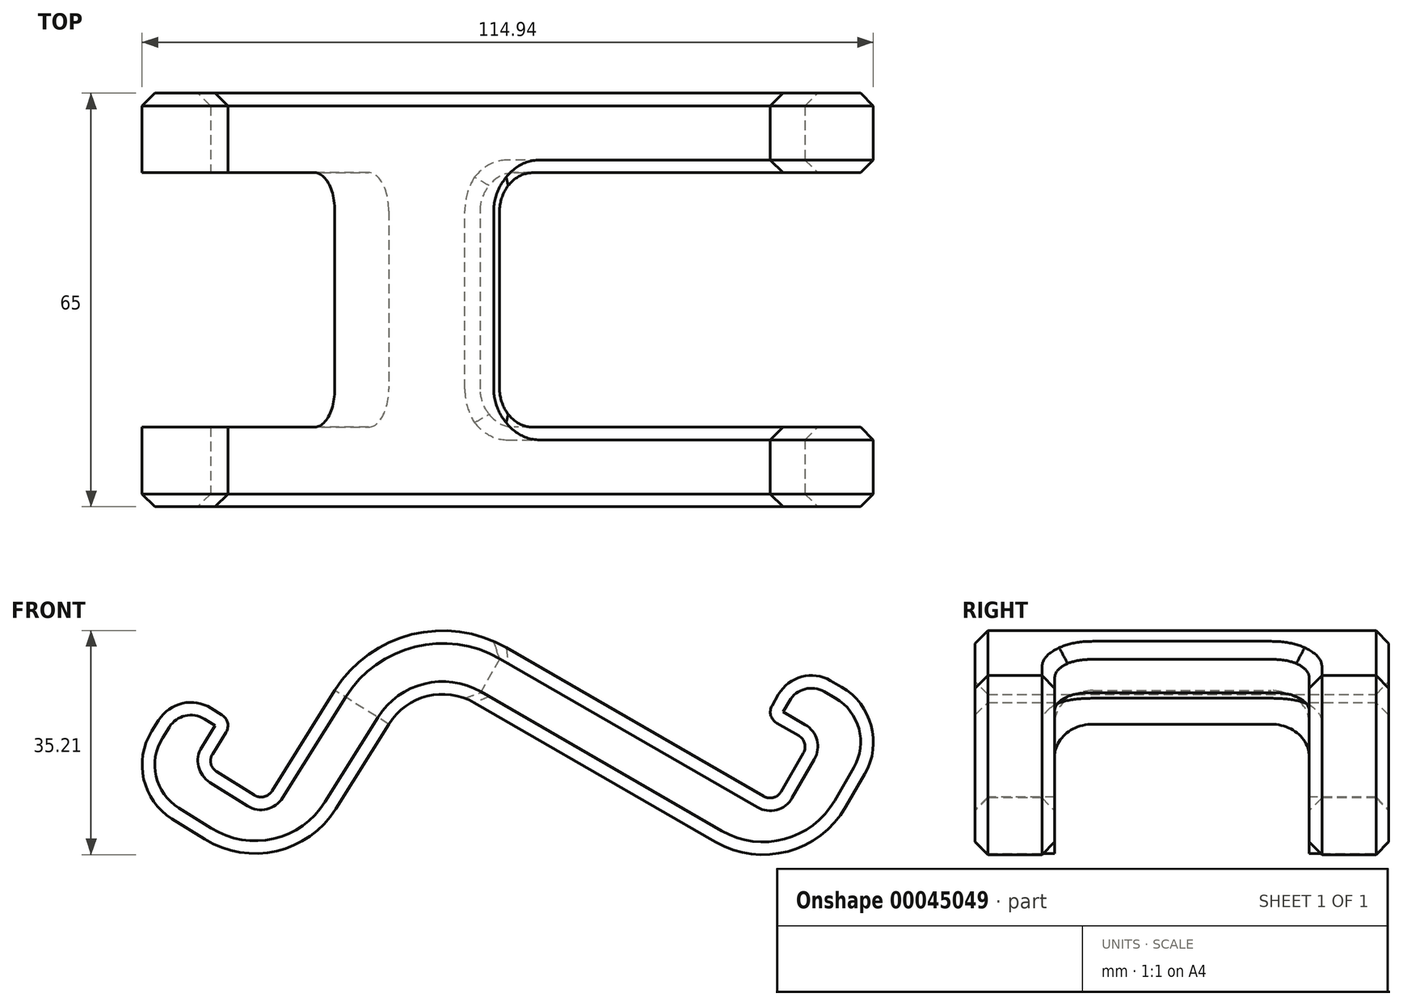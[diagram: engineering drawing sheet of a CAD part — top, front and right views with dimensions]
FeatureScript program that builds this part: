
annotation { "Feature Type Name" : "Feature", "Feature Type Description" : "" }
export const myFeature = defineFeature(function(context is Context, id is Id, definition is map)
    precondition{}
    {
        {
            var Q0;
            Q0=qCreatedBy(makeId("Front.planeOp"),FACE);
            var sketch = newSketch(context, id + "F0", { "sketchPlane" : qUnion([Q0])});
            skLineSegment(sketch, "E0", {"start": v(-41.48, 31.7) * mm, "end": v(-45.72, 24.9) * mm});
            skLineSegment(sketch, "E1", {"start": v(-42.54, 11.13) * mm, "end": v(-37.45, 7.95) * mm});
            skLineSegment(sketch, "E2", {"start": v(-16.78, 12.72) * mm, "end": v(-8.48, 26) * mm});
            skLineSegment(sketch, "E3", {"start": v(5, 29.36) * mm, "end": v(42.87, 7.5) * mm});
            skLineSegment(sketch, "E4", {"start": v(63.36, 13) * mm, "end": v(66.36, 18.19) * mm});
            skLineSegment(sketch, "E5", {"start": v(62.7, 31.85) * mm, "end": v(55.77, 35.85) * mm});
            skLineSegment(sketch, "E6", {"start": v(55.77, 35.85) * mm, "end": v(50.77, 27.19) * mm});
            skLineSegment(sketch, "E7", {"start": v(50.77, 27.19) * mm, "end": v(57.7, 23.19) * mm});
            skLineSegment(sketch, "E8", {"start": v(57.7, 23.19) * mm, "end": v(52.2, 13.66) * mm});
            skLineSegment(sketch, "E9", {"start": v(52.2, 13.66) * mm, "end": v(10, 38.02) * mm});
            skLineSegment(sketch, "E10", {"start": v(-16.96, 31.3) * mm, "end": v(-27.9, 13.78) * mm});
            skLineSegment(sketch, "E11", {"start": v(-27.9, 13.78) * mm, "end": v(-37.24, 19.6) * mm});
            skLineSegment(sketch, "E12", {"start": v(-37.24, 19.6) * mm, "end": v(-33, 26.4) * mm});
            skLineSegment(sketch, "E13", {"start": v(-33, 26.4) * mm, "end": v(-41.48, 31.7) * mm});
            skPoint(sketch, "E14.visualSharp", {"position": v(-6.73, 47.68) * mm});
            skArc(sketch, "E14.filletArc", {"start": v(10, 38.02) * mm, "mid": v(-4.84, 40.1) * mm, "end": v(-16.96, 31.3) * mm});
            skPoint(sketch, "E15.visualSharp", {"position": v(-3.36, 34.19) * mm});
            skArc(sketch, "E15.filletArc", {"start": v(5, 29.36) * mm, "mid": v(-2.42, 30.4) * mm, "end": v(-8.48, 26) * mm});
            skPoint(sketch, "E16.visualSharp", {"position": v(55.86, 0) * mm});
            skArc(sketch, "E16.filletArc", {"start": v(42.87, 7.5) * mm, "mid": v(54.25, 6) * mm, "end": v(63.36, 13) * mm});
            skPoint(sketch, "E17.visualSharp", {"position": v(-24.73, 0) * mm});
            skArc(sketch, "E17.filletArc", {"start": v(-37.45, 7.95) * mm, "mid": v(-26.13, 6.05) * mm, "end": v(-16.78, 12.72) * mm});
            skPoint(sketch, "E18.visualSharp", {"position": v(-51.02, 16.43) * mm});
            skArc(sketch, "E18.filletArc", {"start": v(-45.72, 24.9) * mm, "mid": v(-46.98, 17.36) * mm, "end": v(-42.54, 11.13) * mm});
            skPoint(sketch, "E19.visualSharp", {"position": v(71.36, 26.85) * mm});
            skArc(sketch, "E19.filletArc", {"start": v(66.36, 18.19) * mm, "mid": v(67.35, 25.77) * mm, "end": v(62.7, 31.85) * mm});
            skSolve(sketch);
        }
        {
            var Q0;
            Q0=qSketchRegion(id+"F0",true);
            extrude(context, id + "F1", {"entities" : qUnion([Q0]), "endBound" : BoundingType.SYMMETRIC, "depth" : 65 * mm});
        }
        {
            var Q0;
            Q0=qCreatedBy(makeId("Front.planeOp"),FACE);
            var sketch = newSketch(context, id + "F2", { "sketchPlane" : qUnion([Q0])});
            skLineSegment(sketch, "E20", {"start": v(5, 29.36) * mm, "end": v(55.86, 0) * mm});
            skLineSegment(sketch, "E21", {"start": v(55.86, 0) * mm, "end": v(71.36, 26.85) * mm});
            skLineSegment(sketch, "E22", {"start": v(71.36, 26.85) * mm, "end": v(20.5, 56.2) * mm});
            skLineSegment(sketch, "E23", {"start": v(20.5, 56.2) * mm, "end": v(5, 29.36) * mm});
            skLineSegment(sketch, "E24", {"start": v(-8.48, 26) * mm, "end": v(-34.77, 42.43) * mm});
            skLineSegment(sketch, "E25", {"start": v(-34.77, 42.43) * mm, "end": v(-51.02, 16.43) * mm});
            skLineSegment(sketch, "E26", {"start": v(-51.02, 16.43) * mm, "end": v(-24.73, 0) * mm});
            skLineSegment(sketch, "E27", {"start": v(-24.73, 0) * mm, "end": v(-8.48, 26) * mm});
            skLineSegment(sketch, "E28", {"start": v(-8.48, 26) * mm, "end": v(-8.48, 26) * mm});
            skLineSegment(sketch, "E29", {"start": v(5, 29.36) * mm, "end": v(5, 29.36) * mm});
            skSolve(sketch);
        }
        {
            var Q0;
            Q0=qSketchRegion(id+"F2",true);
            extrude(context, id + "F3", {"entities" : qUnion([Q0]), "operationType" : NewBodyOperationType.REMOVE, "endBound" : BoundingType.SYMMETRIC, "oppositeDirection" : true, "depth" : 40 * mm});
        }
        {
            var Q0;
            {var subQ0=sQuery(id+"F0.wireOp",EDGE,"E8");var subQ1=sQuery(id+"F0.wireOp",EDGE,"E9");Q0=makeQuery(id+"F3.boolean.opBoolean","SPLIT",EDGE,{"disambiguationData":[TD([makeQuery(id+"F3.opExtrude","CAP_FACE",FACE,{"disambiguationData":[OSD([sQuery(id+"F2.wireOp",EDGE,"E20"),sQuery(id+"F2.wireOp",EDGE,"E21"),sQuery(id+"F2.wireOp",EDGE,"E22"),sQuery(id+"F2.wireOp",EDGE,"E23")])],"isStart":false})])],"derivedFrom":makeQuery(id+"F1.opExtrude","SWEPT_EDGE",EDGE,{"disambiguationData":[OSD([subQ0,subQ1])]})});}
            var Q1;
            {var subQ0=sQuery(id+"F0.wireOp",EDGE,"E8");var subQ1=sQuery(id+"F0.wireOp",EDGE,"E9");Q1=makeQuery(id+"F3.boolean.opBoolean","SPLIT",EDGE,{"disambiguationData":[TD([makeQuery(id+"F3.opExtrude","CAP_FACE",FACE,{"disambiguationData":[OSD([sQuery(id+"F2.wireOp",EDGE,"E20"),sQuery(id+"F2.wireOp",EDGE,"E21"),sQuery(id+"F2.wireOp",EDGE,"E22"),sQuery(id+"F2.wireOp",EDGE,"E23")])],"isStart":true})])],"derivedFrom":makeQuery(id+"F1.opExtrude","SWEPT_EDGE",EDGE,{"disambiguationData":[OSD([subQ0,subQ1])]})});}
            var Q2;
            {var subQ0=sQuery(id+"F0.wireOp",EDGE,"E7");var subQ1=sQuery(id+"F0.wireOp",EDGE,"E8");Q2=makeQuery(id+"F3.boolean.opBoolean","SPLIT",EDGE,{"disambiguationData":[TD([makeQuery(id+"F3.opExtrude","CAP_FACE",FACE,{"disambiguationData":[OSD([sQuery(id+"F2.wireOp",EDGE,"E20"),sQuery(id+"F2.wireOp",EDGE,"E21"),sQuery(id+"F2.wireOp",EDGE,"E22"),sQuery(id+"F2.wireOp",EDGE,"E23")])],"isStart":true})])],"derivedFrom":makeQuery(id+"F1.opExtrude","SWEPT_EDGE",EDGE,{"disambiguationData":[OSD([subQ0,subQ1])]})});}
            var Q3;
            {var subQ0=sQuery(id+"F0.wireOp",EDGE,"E7");var subQ1=sQuery(id+"F0.wireOp",EDGE,"E8");Q3=makeQuery(id+"F3.boolean.opBoolean","SPLIT",EDGE,{"disambiguationData":[TD([makeQuery(id+"F3.opExtrude","CAP_FACE",FACE,{"disambiguationData":[OSD([sQuery(id+"F2.wireOp",EDGE,"E20"),sQuery(id+"F2.wireOp",EDGE,"E21"),sQuery(id+"F2.wireOp",EDGE,"E22"),sQuery(id+"F2.wireOp",EDGE,"E23")])],"isStart":false})])],"derivedFrom":makeQuery(id+"F1.opExtrude","SWEPT_EDGE",EDGE,{"disambiguationData":[OSD([subQ0,subQ1])]})});}
            var Q4;
            {var subQ0=sQuery(id+"F0.wireOp",EDGE,"E10");var subQ1=sQuery(id+"F0.wireOp",EDGE,"E11");Q4=makeQuery(id+"F3.boolean.opBoolean","SPLIT",EDGE,{"disambiguationData":[TD([makeQuery(id+"F3.opExtrude","CAP_FACE",FACE,{"disambiguationData":[OSD([sQuery(id+"F2.wireOp",EDGE,"E24"),sQuery(id+"F2.wireOp",EDGE,"E25"),sQuery(id+"F2.wireOp",EDGE,"E26"),sQuery(id+"F2.wireOp",EDGE,"E27")])],"isStart":true})])],"derivedFrom":makeQuery(id+"F1.opExtrude","SWEPT_EDGE",EDGE,{"disambiguationData":[OSD([subQ0,subQ1])]})});}
            var Q5;
            {var subQ0=sQuery(id+"F0.wireOp",EDGE,"E10");var subQ1=sQuery(id+"F0.wireOp",EDGE,"E11");Q5=makeQuery(id+"F3.boolean.opBoolean","SPLIT",EDGE,{"disambiguationData":[TD([makeQuery(id+"F3.opExtrude","CAP_FACE",FACE,{"disambiguationData":[OSD([sQuery(id+"F2.wireOp",EDGE,"E24"),sQuery(id+"F2.wireOp",EDGE,"E25"),sQuery(id+"F2.wireOp",EDGE,"E26"),sQuery(id+"F2.wireOp",EDGE,"E27")])],"isStart":false})])],"derivedFrom":makeQuery(id+"F1.opExtrude","SWEPT_EDGE",EDGE,{"disambiguationData":[OSD([subQ0,subQ1])]})});}
            var Q6;
            {var subQ0=sQuery(id+"F0.wireOp",EDGE,"E11");var subQ1=sQuery(id+"F0.wireOp",EDGE,"E12");Q6=makeQuery(id+"F3.boolean.opBoolean","SPLIT",EDGE,{"disambiguationData":[TD([makeQuery(id+"F3.opExtrude","CAP_FACE",FACE,{"disambiguationData":[OSD([sQuery(id+"F2.wireOp",EDGE,"E24"),sQuery(id+"F2.wireOp",EDGE,"E25"),sQuery(id+"F2.wireOp",EDGE,"E26"),sQuery(id+"F2.wireOp",EDGE,"E27")])],"isStart":true})])],"derivedFrom":makeQuery(id+"F1.opExtrude","SWEPT_EDGE",EDGE,{"disambiguationData":[OSD([subQ0,subQ1])]})});}
            var Q7;
            {var subQ0=sQuery(id+"F0.wireOp",EDGE,"E12");var subQ1=sQuery(id+"F0.wireOp",EDGE,"E13");Q7=makeQuery(id+"F3.boolean.opBoolean","SPLIT",EDGE,{"disambiguationData":[TD([makeQuery(id+"F3.opExtrude","CAP_FACE",FACE,{"disambiguationData":[OSD([sQuery(id+"F2.wireOp",EDGE,"E24"),sQuery(id+"F2.wireOp",EDGE,"E25"),sQuery(id+"F2.wireOp",EDGE,"E26"),sQuery(id+"F2.wireOp",EDGE,"E27")])],"isStart":true})])],"derivedFrom":makeQuery(id+"F1.opExtrude","SWEPT_EDGE",EDGE,{"disambiguationData":[OSD([subQ0,subQ1])]})});}
            var Q8;
            {var subQ0=sQuery(id+"F0.wireOp",EDGE,"E12");var subQ1=sQuery(id+"F0.wireOp",EDGE,"E13");Q8=makeQuery(id+"F3.boolean.opBoolean","SPLIT",EDGE,{"disambiguationData":[TD([makeQuery(id+"F3.opExtrude","CAP_FACE",FACE,{"disambiguationData":[OSD([sQuery(id+"F2.wireOp",EDGE,"E24"),sQuery(id+"F2.wireOp",EDGE,"E25"),sQuery(id+"F2.wireOp",EDGE,"E26"),sQuery(id+"F2.wireOp",EDGE,"E27")])],"isStart":false})])],"derivedFrom":makeQuery(id+"F1.opExtrude","SWEPT_EDGE",EDGE,{"disambiguationData":[OSD([subQ0,subQ1])]})});}
            var Q9;
            {var subQ0=sQuery(id+"F0.wireOp",EDGE,"E6");var subQ1=sQuery(id+"F0.wireOp",EDGE,"E7");Q9=makeQuery(id+"F3.boolean.opBoolean","SPLIT",EDGE,{"disambiguationData":[TD([makeQuery(id+"F3.opExtrude","CAP_FACE",FACE,{"disambiguationData":[OSD([sQuery(id+"F2.wireOp",EDGE,"E20"),sQuery(id+"F2.wireOp",EDGE,"E21"),sQuery(id+"F2.wireOp",EDGE,"E22"),sQuery(id+"F2.wireOp",EDGE,"E23")])],"isStart":false})])],"derivedFrom":makeQuery(id+"F1.opExtrude","SWEPT_EDGE",EDGE,{"disambiguationData":[OSD([subQ0,subQ1])]})});}
            var Q10;
            {var subQ0=sQuery(id+"F0.wireOp",EDGE,"E6");var subQ1=sQuery(id+"F0.wireOp",EDGE,"E7");Q10=makeQuery(id+"F3.boolean.opBoolean","SPLIT",EDGE,{"disambiguationData":[TD([makeQuery(id+"F3.opExtrude","CAP_FACE",FACE,{"disambiguationData":[OSD([sQuery(id+"F2.wireOp",EDGE,"E20"),sQuery(id+"F2.wireOp",EDGE,"E21"),sQuery(id+"F2.wireOp",EDGE,"E22"),sQuery(id+"F2.wireOp",EDGE,"E23")])],"isStart":true})])],"derivedFrom":makeQuery(id+"F1.opExtrude","SWEPT_EDGE",EDGE,{"disambiguationData":[OSD([subQ0,subQ1])]})});}
            var Q11;
            {var subQ0=sQuery(id+"F0.wireOp",EDGE,"E11");var subQ1=sQuery(id+"F0.wireOp",EDGE,"E12");Q11=makeQuery(id+"F3.boolean.opBoolean","SPLIT",EDGE,{"disambiguationData":[TD([makeQuery(id+"F3.opExtrude","CAP_FACE",FACE,{"disambiguationData":[OSD([sQuery(id+"F2.wireOp",EDGE,"E24"),sQuery(id+"F2.wireOp",EDGE,"E25"),sQuery(id+"F2.wireOp",EDGE,"E26"),sQuery(id+"F2.wireOp",EDGE,"E27")])],"isStart":false})])],"derivedFrom":makeQuery(id+"F1.opExtrude","SWEPT_EDGE",EDGE,{"disambiguationData":[OSD([subQ0,subQ1])]})});}
            fillet(context, id + "F4", {"entities" : qUnion([Q0, Q1, Q2, Q3, Q4, Q5, Q6, Q7, Q8, Q9, Q10, Q11]), "radius" : 2 * mm, "tangentPropagation" : true, "allowEdgeOverflow" : false});
        }
        {
            var Q0;
            {var subQ0=sQuery(id+"F0.wireOp",EDGE,"E0");var subQ1=sQuery(id+"F0.wireOp",EDGE,"E13");Q0=makeQuery(id+"F3.boolean.opBoolean","SPLIT",EDGE,{"disambiguationData":[TD([makeQuery(id+"F3.opExtrude","CAP_FACE",FACE,{"disambiguationData":[OSD([sQuery(id+"F2.wireOp",EDGE,"E24"),sQuery(id+"F2.wireOp",EDGE,"E25"),sQuery(id+"F2.wireOp",EDGE,"E26"),sQuery(id+"F2.wireOp",EDGE,"E27")])],"isStart":true})])],"derivedFrom":makeQuery(id+"F1.opExtrude","SWEPT_EDGE",EDGE,{"disambiguationData":[OSD([subQ0,subQ1])]})});}
            var Q1;
            {var subQ0=sQuery(id+"F0.wireOp",EDGE,"E0");var subQ1=sQuery(id+"F0.wireOp",EDGE,"E13");Q1=makeQuery(id+"F3.boolean.opBoolean","SPLIT",EDGE,{"disambiguationData":[TD([makeQuery(id+"F3.opExtrude","CAP_FACE",FACE,{"disambiguationData":[OSD([sQuery(id+"F2.wireOp",EDGE,"E24"),sQuery(id+"F2.wireOp",EDGE,"E25"),sQuery(id+"F2.wireOp",EDGE,"E26"),sQuery(id+"F2.wireOp",EDGE,"E27")])],"isStart":false})])],"derivedFrom":makeQuery(id+"F1.opExtrude","SWEPT_EDGE",EDGE,{"disambiguationData":[OSD([subQ0,subQ1])]})});}
            var Q2;
            {var subQ0=sQuery(id+"F0.wireOp",EDGE,"E5");var subQ1=sQuery(id+"F0.wireOp",EDGE,"E6");Q2=makeQuery(id+"F3.boolean.opBoolean","SPLIT",EDGE,{"disambiguationData":[TD([makeQuery(id+"F3.opExtrude","CAP_FACE",FACE,{"disambiguationData":[OSD([sQuery(id+"F2.wireOp",EDGE,"E20"),sQuery(id+"F2.wireOp",EDGE,"E21"),sQuery(id+"F2.wireOp",EDGE,"E22"),sQuery(id+"F2.wireOp",EDGE,"E23")])],"isStart":false})])],"derivedFrom":makeQuery(id+"F1.opExtrude","SWEPT_EDGE",EDGE,{"disambiguationData":[OSD([subQ0,subQ1])]})});}
            var Q3;
            {var subQ0=sQuery(id+"F0.wireOp",EDGE,"E5");var subQ1=sQuery(id+"F0.wireOp",EDGE,"E6");Q3=makeQuery(id+"F3.boolean.opBoolean","SPLIT",EDGE,{"disambiguationData":[TD([makeQuery(id+"F3.opExtrude","CAP_FACE",FACE,{"disambiguationData":[OSD([sQuery(id+"F2.wireOp",EDGE,"E20"),sQuery(id+"F2.wireOp",EDGE,"E21"),sQuery(id+"F2.wireOp",EDGE,"E22"),sQuery(id+"F2.wireOp",EDGE,"E23")])],"isStart":true})])],"derivedFrom":makeQuery(id+"F1.opExtrude","SWEPT_EDGE",EDGE,{"disambiguationData":[OSD([subQ0,subQ1])]})});}
            fillet(context, id + "F5", {"entities" : qUnion([Q0, Q1, Q2, Q3]), "radius" : 6 * mm, "tangentPropagation" : true, "allowEdgeOverflow" : false});
        }
        {
            var Q0;
            Q0=makeQuery(id+"F3.boolean.opBoolean","COPY",EDGE,{"derivedFrom":makeQuery(id+"F3.opExtrude","CAP_EDGE",EDGE,{"disambiguationData":[OSD([sQuery(id+"F2.wireOp",EDGE,"E23")])],"isStart":true})});
            var Q1;
            Q1=makeQuery(id+"F3.boolean.opBoolean","COPY",EDGE,{"derivedFrom":makeQuery(id+"F3.opExtrude","CAP_EDGE",EDGE,{"disambiguationData":[OSD([sQuery(id+"F2.wireOp",EDGE,"E23")])],"isStart":false})});
            var Q2;
            Q2=makeQuery(id+"F3.boolean.opBoolean","COPY",EDGE,{"derivedFrom":makeQuery(id+"F3.opExtrude","CAP_EDGE",EDGE,{"disambiguationData":[OSD([sQuery(id+"F2.wireOp",EDGE,"E24")])],"isStart":true})});
            var Q3;
            Q3=makeQuery(id+"F3.boolean.opBoolean","COPY",EDGE,{"derivedFrom":makeQuery(id+"F3.opExtrude","CAP_EDGE",EDGE,{"disambiguationData":[OSD([sQuery(id+"F2.wireOp",EDGE,"E24")])],"isStart":false})});
            fillet(context, id + "F6", {"entities" : qUnion([Q0, Q1, Q2, Q3]), "radius" : 6 * mm, "tangentPropagation" : true, "allowEdgeOverflow" : false});
        }
        {
            var Q0;
            Q0=makeQuery(id+"F3.boolean.opBoolean","INTERSECT",EDGE,{"derivedFrom":[makeQuery(id+"F1.opExtrude","SWEPT_FACE",FACE,{"disambiguationData":[OSD([sQuery(id+"F0.wireOp",EDGE,"E9")])]}),makeQuery(id+"F3.opExtrude","CAP_FACE",FACE,{"disambiguationData":[OSD([sQuery(id+"F2.wireOp",EDGE,"E20"),sQuery(id+"F2.wireOp",EDGE,"E21"),sQuery(id+"F2.wireOp",EDGE,"E22"),sQuery(id+"F2.wireOp",EDGE,"E23")])],"isStart":true})]});
            var Q1;
            Q1=makeQuery(id+"F3.boolean.opBoolean","INTERSECT",EDGE,{"derivedFrom":[makeQuery(id+"F1.opExtrude","SWEPT_FACE",FACE,{"disambiguationData":[OSD([sQuery(id+"F0.wireOp",EDGE,"E8")])]}),makeQuery(id+"F3.opExtrude","CAP_FACE",FACE,{"disambiguationData":[OSD([sQuery(id+"F2.wireOp",EDGE,"E20"),sQuery(id+"F2.wireOp",EDGE,"E21"),sQuery(id+"F2.wireOp",EDGE,"E22"),sQuery(id+"F2.wireOp",EDGE,"E23")])],"isStart":true})]});
            var Q2;
            {var subQ0=sQuery(id+"F0.wireOp",EDGE,"E8");var subQ1=sQuery(id+"F0.wireOp",EDGE,"E9");var subQ2=makeQuery(id+"F3.opExtrude","CAP_FACE",FACE,{"disambiguationData":[OSD([sQuery(id+"F2.wireOp",EDGE,"E20"),sQuery(id+"F2.wireOp",EDGE,"E21"),sQuery(id+"F2.wireOp",EDGE,"E22"),sQuery(id+"F2.wireOp",EDGE,"E23")])],"isStart":true});Q2=makeQuery(id+"F4.opFillet","BLEND_EDGE",EDGE,{"blendedFrom":[makeQuery(id+"F3.boolean.opBoolean","SPLIT",EDGE,{"disambiguationData":[TD([subQ2])],"derivedFrom":makeQuery(id+"F1.opExtrude","SWEPT_EDGE",EDGE,{"disambiguationData":[OSD([subQ0,subQ1])]})}),makeQuery(id+"F3.boolean.opBoolean","COPY",FACE,{"derivedFrom":subQ2})],"blendedInto":[makeQuery(id+"F3.boolean.opBoolean","COPY",FACE,{"derivedFrom":subQ2})]});}
            var Q3;
            Q3=makeQuery(id+"F6.opFillet","BLEND_EDGE",EDGE,{"blendedFrom":[makeQuery(id+"F3.boolean.opBoolean","COPY",EDGE,{"derivedFrom":makeQuery(id+"F3.opExtrude","CAP_EDGE",EDGE,{"disambiguationData":[OSD([sQuery(id+"F2.wireOp",EDGE,"E23")])],"isStart":true})}),makeQuery(id+"F1.opExtrude","SWEPT_FACE",FACE,{"disambiguationData":[OSD([sQuery(id+"F0.wireOp",EDGE,"E9")])]})],"blendedInto":[makeQuery(id+"F1.opExtrude","SWEPT_FACE",FACE,{"disambiguationData":[OSD([sQuery(id+"F0.wireOp",EDGE,"E9")])]})]});
            var Q4;
            Q4=makeQuery(id+"F3.boolean.opBoolean","INTERSECT",EDGE,{"derivedFrom":[makeQuery(id+"F1.opExtrude","SWEPT_FACE",FACE,{"disambiguationData":[OSD([sQuery(id+"F0.wireOp",EDGE,"E9")])]}),makeQuery(id+"F3.opExtrude","SWEPT_FACE",FACE,{"disambiguationData":[OSD([sQuery(id+"F2.wireOp",EDGE,"E23")])]})]});
            var Q5;
            Q5=makeQuery(id+"F6.opFillet","BLEND_EDGE",EDGE,{"blendedFrom":[makeQuery(id+"F3.boolean.opBoolean","COPY",EDGE,{"derivedFrom":makeQuery(id+"F3.opExtrude","CAP_EDGE",EDGE,{"disambiguationData":[OSD([sQuery(id+"F2.wireOp",EDGE,"E23")])],"isStart":false})}),makeQuery(id+"F1.opExtrude","SWEPT_FACE",FACE,{"disambiguationData":[OSD([sQuery(id+"F0.wireOp",EDGE,"E9")])]})],"blendedInto":[makeQuery(id+"F1.opExtrude","SWEPT_FACE",FACE,{"disambiguationData":[OSD([sQuery(id+"F0.wireOp",EDGE,"E9")])]})]});
            var Q6;
            Q6=makeQuery(id+"F3.boolean.opBoolean","INTERSECT",EDGE,{"derivedFrom":[makeQuery(id+"F1.opExtrude","SWEPT_FACE",FACE,{"disambiguationData":[OSD([sQuery(id+"F0.wireOp",EDGE,"E9")])]}),makeQuery(id+"F3.opExtrude","CAP_FACE",FACE,{"disambiguationData":[OSD([sQuery(id+"F2.wireOp",EDGE,"E20"),sQuery(id+"F2.wireOp",EDGE,"E21"),sQuery(id+"F2.wireOp",EDGE,"E22"),sQuery(id+"F2.wireOp",EDGE,"E23")])],"isStart":false})]});
            var Q7;
            {var subQ0=sQuery(id+"F0.wireOp",EDGE,"E8");var subQ1=sQuery(id+"F0.wireOp",EDGE,"E9");var subQ2=makeQuery(id+"F3.opExtrude","CAP_FACE",FACE,{"disambiguationData":[OSD([sQuery(id+"F2.wireOp",EDGE,"E20"),sQuery(id+"F2.wireOp",EDGE,"E21"),sQuery(id+"F2.wireOp",EDGE,"E22"),sQuery(id+"F2.wireOp",EDGE,"E23")])],"isStart":false});Q7=makeQuery(id+"F4.opFillet","BLEND_EDGE",EDGE,{"blendedFrom":[makeQuery(id+"F3.boolean.opBoolean","SPLIT",EDGE,{"disambiguationData":[TD([subQ2])],"derivedFrom":makeQuery(id+"F1.opExtrude","SWEPT_EDGE",EDGE,{"disambiguationData":[OSD([subQ0,subQ1])]})}),makeQuery(id+"F3.boolean.opBoolean","COPY",FACE,{"derivedFrom":subQ2})],"blendedInto":[makeQuery(id+"F3.boolean.opBoolean","COPY",FACE,{"derivedFrom":subQ2})]});}
            var Q8;
            Q8=makeQuery(id+"F3.boolean.opBoolean","INTERSECT",EDGE,{"derivedFrom":[makeQuery(id+"F1.opExtrude","SWEPT_FACE",FACE,{"disambiguationData":[OSD([sQuery(id+"F0.wireOp",EDGE,"E8")])]}),makeQuery(id+"F3.opExtrude","CAP_FACE",FACE,{"disambiguationData":[OSD([sQuery(id+"F2.wireOp",EDGE,"E20"),sQuery(id+"F2.wireOp",EDGE,"E21"),sQuery(id+"F2.wireOp",EDGE,"E22"),sQuery(id+"F2.wireOp",EDGE,"E23")])],"isStart":false})]});
            var Q9;
            Q9=makeQuery(id+"F3.boolean.opBoolean","INTERSECT",EDGE,{"derivedFrom":[makeQuery(id+"F1.opExtrude","SWEPT_FACE",FACE,{"disambiguationData":[OSD([sQuery(id+"F0.wireOp",EDGE,"E10")])]}),makeQuery(id+"F3.opExtrude","SWEPT_FACE",FACE,{"disambiguationData":[OSD([sQuery(id+"F2.wireOp",EDGE,"E24")])]})]});
            var Q10;
            Q10=makeQuery(id+"F1.opExtrude","CAP_EDGE",EDGE,{"disambiguationData":[OSD([sQuery(id+"F0.wireOp",EDGE,"E15.filletArc")])],"isStart":false});
            var Q11;
            Q11=makeQuery(id+"F1.opExtrude","CAP_EDGE",EDGE,{"disambiguationData":[OSD([sQuery(id+"F0.wireOp",EDGE,"E15.filletArc")])],"isStart":true});
            chamfer(context, id + "F7", {"entities" : qUnion([Q0, Q1, Q2, Q3, Q4, Q5, Q6, Q7, Q8, Q9, Q10, Q11]), "width" : 2 * mm, "tangentPropagation" : true});
        }
    });
